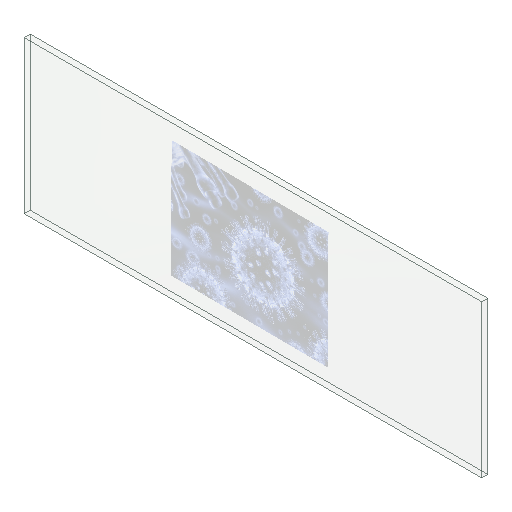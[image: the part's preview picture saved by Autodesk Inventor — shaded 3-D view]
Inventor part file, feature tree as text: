
AUTODESK INVENTOR PART (.ipt)
format: ipt  version: 2022 (Build 260153000, 153)  size: 4,361,728 bytes
history: native  units: mm
features: other x2, sketch x2, extrude x1
ambient origin geometry x8: Origin, YZ Plane, XZ Plane, XY Plane, X Axis, Y Axis, Z Axis, Center Point
bodies: Solid1 (feature_tree)
feature tree (5):
  extrude  "Extrusion1"  Depth=25.0mm
  other  "Decal1"
  sketch  "Sketch1"  dims[d0=75.0mm d1=25.0mm]
  sketch  "Sketch2"  dims[d2=1.0mm d3=0.0mm]
  other  "Image2"
